AUTODESK INVENTOR PART (.ipt)
format: ipt  version: 2016 (Build 200138000, 138)  size: 88,064 bytes
history: native  units: in
note: dims shown in document units (in); Inventor stores cm internally (conversion verified against a paired STEP export)
features: other x9, sketch x2
ambient origin geometry x8: Origin, YZ Plane, XZ Plane, XY Plane, X Axis, Y Axis, Z Axis, Center Point
feature tree (11):
  other  "Blocks"
  sketch  "Sketch1"  dims[d0=2.3622in]
  sketch  "Sketch2"  dims[d1=11.811in d2=9.4488in d5=1.9291in d6=5.9055in d11=2.3622in d12=1.9291in d13=1.5748in]
  other  "L1_legs"
  other  "L2_foot"
  other  "L3_ankle"
  other  "L1_legs:1"
  other  "L2_foot:1"
  other  "L2_foot:2"
  other  "L3_ankle:1"
  other  "L3_ankle:2"
